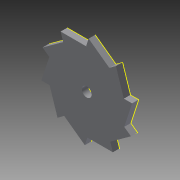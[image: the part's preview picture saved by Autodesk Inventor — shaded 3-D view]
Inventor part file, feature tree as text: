
AUTODESK INVENTOR PART (.ipt)
format: ipt  version: 2013 (Build 170138000, 138)  size: 115,200 bytes
history: native  units: in
note: dims shown in document units (in); Inventor stores cm internally (conversion verified against a paired STEP export)
features: sketch x2, extrude x1
ambient origin geometry x8: Origin, YZ Plane, XZ Plane, XY Plane, X Axis, Y Axis, Z Axis, Center Point
bodies: Solid1 (feature_tree)
feature tree (3):
  extrude  "Extrusion1"  Depth=3.0in
  sketch  "Sketch2"  dims[d2=1.0in d3=3.937in d5=360.0deg d7=0.25in d8=0.0in]
  sketch  "Sketch1"  dims[d0=0.375in d1=3.0in]
